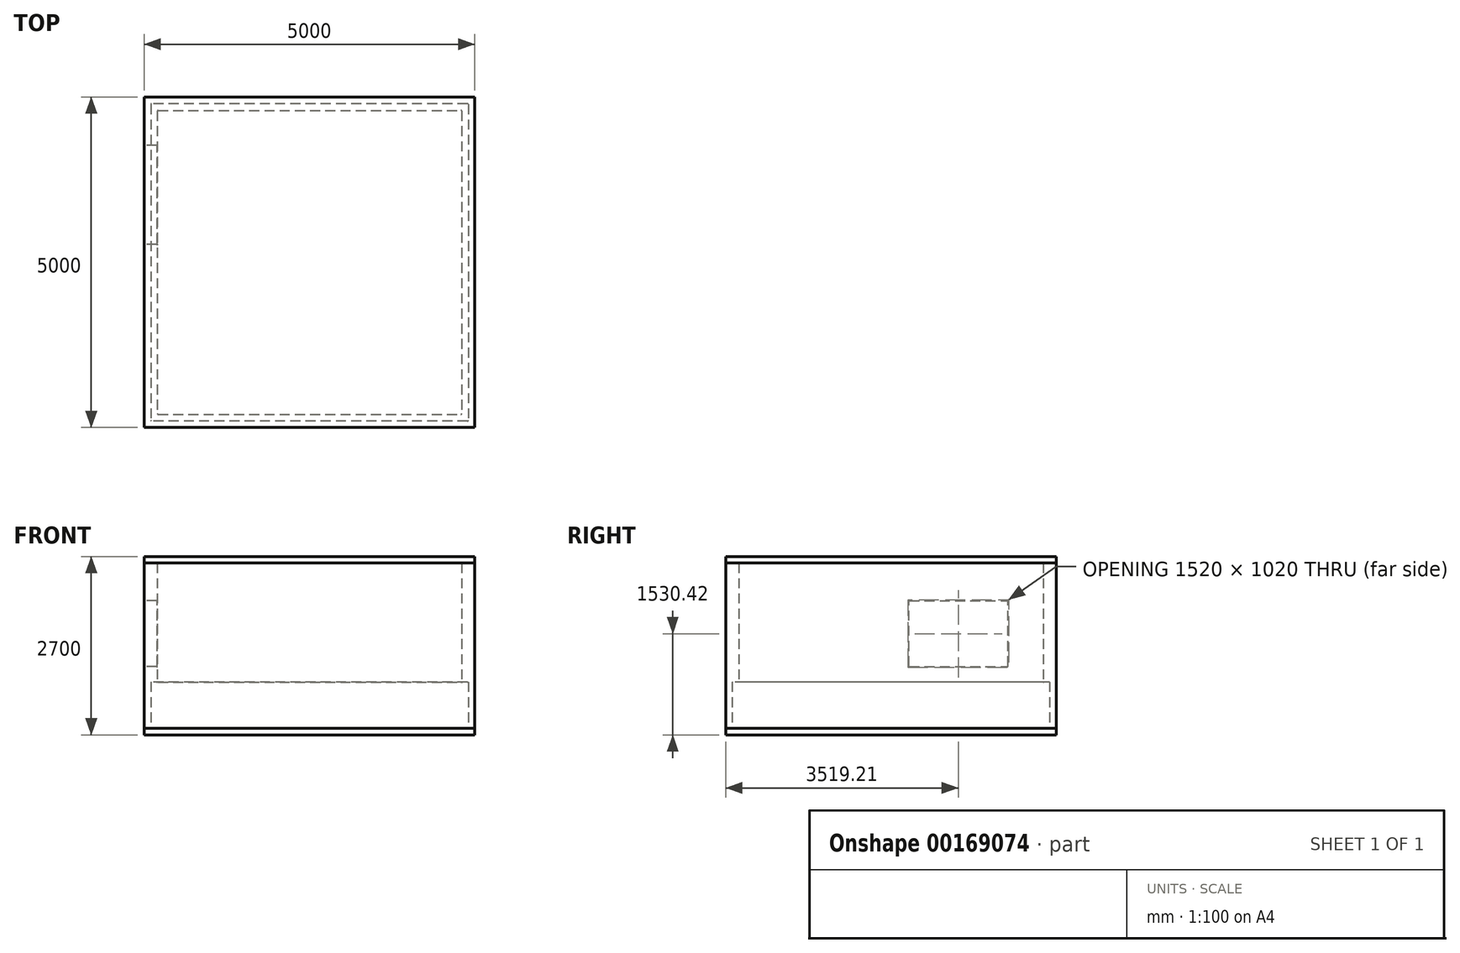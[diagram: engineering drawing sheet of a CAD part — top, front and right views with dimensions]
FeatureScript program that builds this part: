
annotation { "Feature Type Name" : "Feature", "Feature Type Description" : "" }
export const myFeature = defineFeature(function(context is Context, id is Id, definition is map)
    precondition{}
    {
        {
            var Q0;
            Q0=qCreatedBy(makeId("Top.planeOp"),FACE);
            var sketch = newSketch(context, id + "F0", { "sketchPlane" : qUnion([Q0])});
            skLineSegment(sketch, "E0.bottom", {"start": v(2500, -2500) * mm, "end": v(-2500, -2500) * mm});
            skLineSegment(sketch, "E0.top", {"start": v(2500, 2500) * mm, "end": v(-2500, 2500) * mm});
            skLineSegment(sketch, "E0.left", {"start": v(2500, -2500) * mm, "end": v(2500, 2500) * mm});
            skLineSegment(sketch, "E0.right", {"start": v(-2500, -2500) * mm, "end": v(-2500, 2500) * mm});
            skPoint(sketch, "E0.middle", {"position": v(0, 0) * mm});
            skSolve(sketch);
        }
        {
            var Q0;
            Q0=makeQuery(id+"F0.imprint","IMPRINT",FACE,{"disambiguationData":[TD([[makeQuery(id+"F0.imprint","IMPRINT",EDGE,{"derivedFrom":sQuery(id+"F0.wireOp",EDGE,"E0.bottom")}),-1.0]])]});
            extrude(context, id + "F1", {"entities" : qUnion([Q0]), "depth" : 100 * mm});
        }
        {
            var Q0;
            Q0=makeQuery(id+"F1.opExtrude","CAP_FACE",FACE,{"disambiguationData":[OSD([sQuery(id+"F0.wireOp",EDGE,"E0.bottom"),sQuery(id+"F0.wireOp",EDGE,"E0.top"),sQuery(id+"F0.wireOp",EDGE,"E0.left"),sQuery(id+"F0.wireOp",EDGE,"E0.right")])],"isStart":false});
            var sketch = newSketch(context, id + "F2", { "sketchPlane" : qUnion([Q0])});
            skLineSegment(sketch, "E1.bottom", {"start": v(2500, 2500) * mm, "end": v(-2500, 2500) * mm});
            skLineSegment(sketch, "E1.top", {"start": v(2500, -2500) * mm, "end": v(-2500, -2500) * mm});
            skLineSegment(sketch, "E1.left", {"start": v(2500, 2500) * mm, "end": v(2500, -2500) * mm});
            skLineSegment(sketch, "E1.right", {"start": v(-2500, 2500) * mm, "end": v(-2500, -2500) * mm});
            skPoint(sketch, "E1.middle", {"position": v(0, 0) * mm});
            skLineSegment(sketch, "E2.0", {"start": v(-2400, 2400) * mm, "end": v(-2400, -2400) * mm});
            skLineSegment(sketch, "E2.1", {"start": v(2400, 2400) * mm, "end": v(-2400, 2400) * mm});
            skLineSegment(sketch, "E2.2", {"start": v(2400, 2400) * mm, "end": v(2400, -2400) * mm});
            skLineSegment(sketch, "E2.3", {"start": v(2400, -2400) * mm, "end": v(-2400, -2400) * mm});
            skSolve(sketch);
        }
        {
            var Q0;
            Q0=makeQuery(id+"F2.imprint","IMPRINT",FACE,{"disambiguationData":[TD([[makeQuery(id+"F2.imprint","IMPRINT",EDGE,{"derivedFrom":sQuery(id+"F2.wireOp",EDGE,"E1.bottom")}),1.0]])]});
            extrude(context, id + "F3", {"entities" : qUnion([Q0]), "depth" : 700 * mm});
        }
        {
            var Q0;
            Q0=makeQuery(id+"F3.opExtrude","CAP_FACE",FACE,{"disambiguationData":[OSD([sQuery(id+"F2.wireOp",EDGE,"E1.bottom"),sQuery(id+"F2.wireOp",EDGE,"E1.top"),sQuery(id+"F2.wireOp",EDGE,"E1.left"),sQuery(id+"F2.wireOp",EDGE,"E1.right"),sQuery(id+"F2.wireOp",EDGE,"E2.0"),sQuery(id+"F2.wireOp",EDGE,"E2.1"),sQuery(id+"F2.wireOp",EDGE,"E2.2"),sQuery(id+"F2.wireOp",EDGE,"E2.3")])],"isStart":false});
            var sketch = newSketch(context, id + "F4", { "sketchPlane" : qUnion([Q0])});
            skLineSegment(sketch, "E3.bottom", {"start": v(-2500, 2500) * mm, "end": v(2500, 2500) * mm});
            skLineSegment(sketch, "E3.top", {"start": v(-2500, -2500) * mm, "end": v(2500, -2500) * mm});
            skLineSegment(sketch, "E3.left", {"start": v(-2500, 2500) * mm, "end": v(-2500, -2500) * mm});
            skLineSegment(sketch, "E3.right", {"start": v(2500, 2500) * mm, "end": v(2500, -2500) * mm});
            skPoint(sketch, "E3.middle", {"position": v(0, 0) * mm});
            skLineSegment(sketch, "E4.0", {"start": v(-2300, 2300) * mm, "end": v(-2300, -2300) * mm});
            skLineSegment(sketch, "E4.1", {"start": v(-2300, 2300) * mm, "end": v(2300, 2300) * mm});
            skLineSegment(sketch, "E4.2", {"start": v(2300, 2300) * mm, "end": v(2300, -2300) * mm});
            skLineSegment(sketch, "E4.3", {"start": v(-2300, -2300) * mm, "end": v(2300, -2300) * mm});
            skSolve(sketch);
        }
        {
            var Q0;
            Q0=makeQuery(id+"F4.imprint","IMPRINT",FACE,{"disambiguationData":[TD([[makeQuery(id+"F4.imprint","IMPRINT",EDGE,{"derivedFrom":sQuery(id+"F4.wireOp",EDGE,"E4.0")}),-1.0]])]});
            var Q1;
            Q1=makeQuery(id+"F4.imprint","IMPRINT",FACE,{"disambiguationData":[TD([[makeQuery(id+"F4.imprint","IMPRINT",EDGE,{"derivedFrom":sQuery(id+"F4.wireOp",EDGE,"E3.bottom")}),1.0]])]});
            extrude(context, id + "F5", {"entities" : qUnion([Q0, Q1]), "operationType" : NewBodyOperationType.ADD, "depth" : 1800 * mm});
        }
        {
            var Q0;
            Q0=makeQuery(id+"F5.opExtrude","CAP_FACE",FACE,{"disambiguationData":[OSD([sQuery(id+"F4.wireOp",EDGE,"E3.bottom"),sQuery(id+"F4.wireOp",EDGE,"E3.top"),sQuery(id+"F4.wireOp",EDGE,"E3.left"),sQuery(id+"F4.wireOp",EDGE,"E3.right"),sQuery(id+"F4.wireOp",EDGE,"E4.0"),sQuery(id+"F4.wireOp",EDGE,"E4.1"),sQuery(id+"F4.wireOp",EDGE,"E4.2"),sQuery(id+"F4.wireOp",EDGE,"E4.3")])],"isStart":false});
            var sketch = newSketch(context, id + "F6", { "sketchPlane" : qUnion([Q0])});
            skLineSegment(sketch, "E5.bottom", {"start": v(2500, 2500) * mm, "end": v(-2500, 2500) * mm});
            skLineSegment(sketch, "E5.top", {"start": v(2500, -2500) * mm, "end": v(-2500, -2500) * mm});
            skLineSegment(sketch, "E5.left", {"start": v(2500, 2500) * mm, "end": v(2500, -2500) * mm});
            skLineSegment(sketch, "E5.right", {"start": v(-2500, 2500) * mm, "end": v(-2500, -2500) * mm});
            skPoint(sketch, "E5.middle", {"position": v(0, 0) * mm});
            skSolve(sketch);
        }
        {
            var Q0;
            Q0=makeQuery(id+"F6.imprint","IMPRINT",FACE,{"disambiguationData":[TD([[makeQuery(id+"F6.imprint","IMPRINT",EDGE,{"derivedFrom":sQuery(id+"F6.wireOp",EDGE,"E5.bottom")}),1.0]])]});
            var Q1;
            Q1=makeQuery(id+"F6.imprint","IMPRINT",FACE,{"disambiguationData":[TD([[makeQuery(id+"F6.imprint","IMPRINT",EDGE,{"derivedFrom":makeQuery(id+"F5.opExtrude","CAP_EDGE",EDGE,{"disambiguationData":[OSD([sQuery(id+"F4.wireOp",EDGE,"E4.0")])],"isStart":false})}),1.0]])]});
            extrude(context, id + "F7", {"entities" : qUnion([Q0, Q1]), "depth" : 100 * mm});
        }
        {
            var Q0;
            Q0=makeQuery(id+"F5.boolean.opBoolean","MERGE",FACE,{"derivedFrom":[makeQuery(id+"F3.opExtrude","SWEPT_FACE",FACE,{"disambiguationData":[OSD([sQuery(id+"F2.wireOp",EDGE,"E1.right")])]}),makeQuery(id+"F5.opExtrude","SWEPT_FACE",FACE,{"disambiguationData":[OSD([sQuery(id+"F4.wireOp",EDGE,"E3.left")])]})]});
            var sketch = newSketch(context, id + "F8", { "sketchPlane" : qUnion([Q0])});
            skLineSegment(sketch, "E6.bottom", {"start": v(-269.2, 1030.42) * mm, "end": v(-1769.2, 1030.42) * mm});
            skLineSegment(sketch, "E6.top", {"start": v(-269.2, 2030.42) * mm, "end": v(-1769.2, 2030.42) * mm});
            skLineSegment(sketch, "E6.left", {"start": v(-269.2, 1030.42) * mm, "end": v(-269.2, 2030.42) * mm});
            skLineSegment(sketch, "E6.right", {"start": v(-1769.2, 1030.42) * mm, "end": v(-1769.2, 2030.42) * mm});
            skPoint(sketch, "E6.middle", {"position": v(-1019.2, 1530.42) * mm});
            skSolve(sketch);
        }
        {
            var Q0;
            Q0 = qSketchRegion(id + "F8", true);
            extrude(context, id + "F9", {"entities" : qUnion([Q0]), "operationType" : NewBodyOperationType.REMOVE, "endBound" : BoundingType.UP_TO_NEXT, "oppositeDirection" : true, "depth" : 25 * mm});
        }
        {
            var Q0;
            Q0=makeQuery(id+"F5.opExtrude","SWEPT_EDGE",EDGE,{"disambiguationData":[OSD([sQuery(id+"F4.wireOp",EDGE,"E4.0"),sQuery(id+"F4.wireOp",EDGE,"E4.1")])]});
            var Q1;
            Q1=makeQuery(id+"F5.opExtrude","SWEPT_EDGE",EDGE,{"disambiguationData":[OSD([sQuery(id+"F4.wireOp",EDGE,"E4.1"),sQuery(id+"F4.wireOp",EDGE,"E4.2")])]});
            var Q2;
            Q2=makeQuery(id+"F5.opExtrude","SWEPT_EDGE",EDGE,{"disambiguationData":[OSD([sQuery(id+"F4.wireOp",EDGE,"E4.2"),sQuery(id+"F4.wireOp",EDGE,"E4.3")])]});
            var Q3;
            Q3=makeQuery(id+"F5.opExtrude","SWEPT_EDGE",EDGE,{"disambiguationData":[OSD([sQuery(id+"F4.wireOp",EDGE,"E4.0"),sQuery(id+"F4.wireOp",EDGE,"E4.3")])]});
            var Q4;
            Q4=makeQuery(id+"F3.opExtrude","SWEPT_EDGE",EDGE,{"disambiguationData":[OSD([sQuery(id+"F2.wireOp",EDGE,"E2.0"),sQuery(id+"F2.wireOp",EDGE,"E2.3")])]});
            var Q5;
            Q5=makeQuery(id+"F3.opExtrude","SWEPT_EDGE",EDGE,{"disambiguationData":[OSD([sQuery(id+"F2.wireOp",EDGE,"E2.0"),sQuery(id+"F2.wireOp",EDGE,"E2.1")])]});
            var Q6;
            Q6=makeQuery(id+"F3.opExtrude","SWEPT_EDGE",EDGE,{"disambiguationData":[OSD([sQuery(id+"F2.wireOp",EDGE,"E2.1"),sQuery(id+"F2.wireOp",EDGE,"E2.2")])]});
            var Q7;
            Q7=makeQuery(id+"F3.opExtrude","SWEPT_EDGE",EDGE,{"disambiguationData":[OSD([sQuery(id+"F2.wireOp",EDGE,"E2.2"),sQuery(id+"F2.wireOp",EDGE,"E2.3")])]});
            fillet(context, id + "F10", {"entities" : qUnion([Q0, Q1, Q2, Q3, Q4, Q5, Q6, Q7]), "radius" : 10 * mm, "tangentPropagation" : true, "allowEdgeOverflow" : false});
        }
        {
            var Q0;
            Q0=makeQuery(id+"F5.opExtrude","CAP_EDGE",EDGE,{"disambiguationData":[OSD([sQuery(id+"F4.wireOp",EDGE,"E4.1")])],"isStart":true});
            var Q1;
            Q1=makeQuery(id+"F3.opExtrude","CAP_EDGE",EDGE,{"disambiguationData":[OSD([sQuery(id+"F2.wireOp",EDGE,"E2.1")])],"isStart":false});
            fillet(context, id + "F11", {"entities" : qUnion([Q0, Q1]), "radius" : 10 * mm, "tangentPropagation" : true, "allowEdgeOverflow" : false});
        }
        {
            var Q0;
            Q0=makeQuery(id+"F9.boolean.opBoolean","COPY",FACE,{"derivedFrom":makeQuery(id+"F9.opExtrude","SWEPT_FACE",FACE,{"disambiguationData":[OSD([sQuery(id+"F8.wireOp",EDGE,"E6.bottom")])]})});
            var Q1;
            Q1=makeQuery(id+"F9.boolean.opBoolean","COPY",FACE,{"derivedFrom":makeQuery(id+"F9.opExtrude","SWEPT_FACE",FACE,{"disambiguationData":[OSD([sQuery(id+"F8.wireOp",EDGE,"E6.right")])]})});
            var Q2;
            Q2=makeQuery(id+"F9.boolean.opBoolean","COPY",FACE,{"derivedFrom":makeQuery(id+"F9.opExtrude","SWEPT_FACE",FACE,{"disambiguationData":[OSD([sQuery(id+"F8.wireOp",EDGE,"E6.left")])]})});
            var Q3;
            Q3=makeQuery(id+"F9.boolean.opBoolean","COPY",FACE,{"derivedFrom":makeQuery(id+"F9.opExtrude","SWEPT_FACE",FACE,{"disambiguationData":[OSD([sQuery(id+"F8.wireOp",EDGE,"E6.top")])]})});
            fillet(context, id + "F12", {"entities" : qUnion([Q0, Q1, Q2, Q3]), "radius" : 10 * mm, "tangentPropagation" : true, "allowEdgeOverflow" : false});
        }
    });
